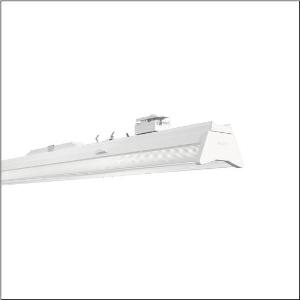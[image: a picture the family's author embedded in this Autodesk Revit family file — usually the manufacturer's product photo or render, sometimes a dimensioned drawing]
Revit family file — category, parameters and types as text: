
# Revit family: licross_11_performance_ho_51td16dn6exm
name_source: partatom
category: Lighting Fixtures
units: mm (PartAtom-declared; Revit-internal decimal feet)

## family parameters
Cut with Voids When Loaded = No
Host = Face
Light Source = No
Part Type = Normal
Room Calculation Point = No
Round Connector Dimension = Use Diameter
Shared = No

## types (1)
- --- (1 x LED, 14180 lm, 81.4 W, 6500K)
    Apparent Load = 81 VA
    CIE Flux Codes = 63 87 95 78 100
    Color Rendering = 80
    Color Temperature = 6500K
    Default Elevation = 1800 mm
    Description = Licross 11 Performance HO, luminaire insert, of sheet steel, galvanised, coil coated, white, length: 1.500mm, width: 120mm, height: 123mm, LED rated luminous flux: 14.180lm, light colour: 865, SDCM (Standard Deviation of Colour Matching)MacAdam ≤ 2 SDCM (initial), control gear: DALI 2, with plug, 5-pole, with phase selection, mains connection: 220..240V, AC, 50/60Hz, rated input power: 81W, internal wiring halogen-free, primary light control with lens, of plastic, primary optical cover: cover, of PMMA, light emission: direct/indirect distribution, primary light characteristic: symmetric, protection rating (complete): IP54, insulation class (complete): insulation class I (protective earthing), certification: CE, ENEC, VDE, UKCA, protection symbol: D if used in an environment with non-conductive dust loads with corresponding accessories, impact resistance: IK06, permissible ambient temperature for indoor applications: -25..+35°C, corresponds to IFS (International Featured Standards) requirements for safety and quality in the food industry, reducing of maximum allowable ambient temperature of 5°C with ceiling mounting, LABS conformity tested according to VDMA 24364:2018-05, The light source and the operating device comply with the requirements of the Ecodesign Regulation (EU) 2019/2020 and are replaceable in accordance with this regulation, packaging unit: 1 piece
    Height = 114 mm
    Lamp = 1 x LED
    Lamp Light Flux = 14180 lm
    Lamp Power = 81.4 W
    Lamp count = 1
    Length = 1500 mm
    Luminous efficacy = 174 lm/W
    Manufacturer = Siteco
    ModVariant = No
    Model = 51TD16DN6EXM
    Mounting Place = Ceiling
    Mounting Type = Pendant
    Number of Poles = 1
    OnlyDefault = Yes
    Power Factor = 1
    Product Name = Licross 11 Performance HO
    Product group = luminaire insert | ceiling pendant
    ProductGroupID = 901
    Protection Class = Protection class I
    Protection Degree = IP 54
    RLX_Detail_Level = 1
    RLX_Emergency_Light_Flux = 0 lm
    RLX_Emergency_Type = 0
    RLX_Emergency_Type_DB = No
    RlxData = <blob elided: 34361 chars, md5=53201f8c>
    Socket = socket
    Standby Power = 0 W
    System Light Flux = 14180 lm
    System Power = 81 W
    Type Comments = factory setting: luminous flux: 100 % | dim-lin: 254 | 550 mA
    Type Image = l_1256138.jpg
    URL = http://relux.com
    VarID = @adj_077341
    Voltage = 0 V
    Weight = 0.00 kg
    Width = 120 mm

## geometry (parser evidence)
native form markers: Blend x4, Sweep x12
no freeform markers — native parametric forms only
